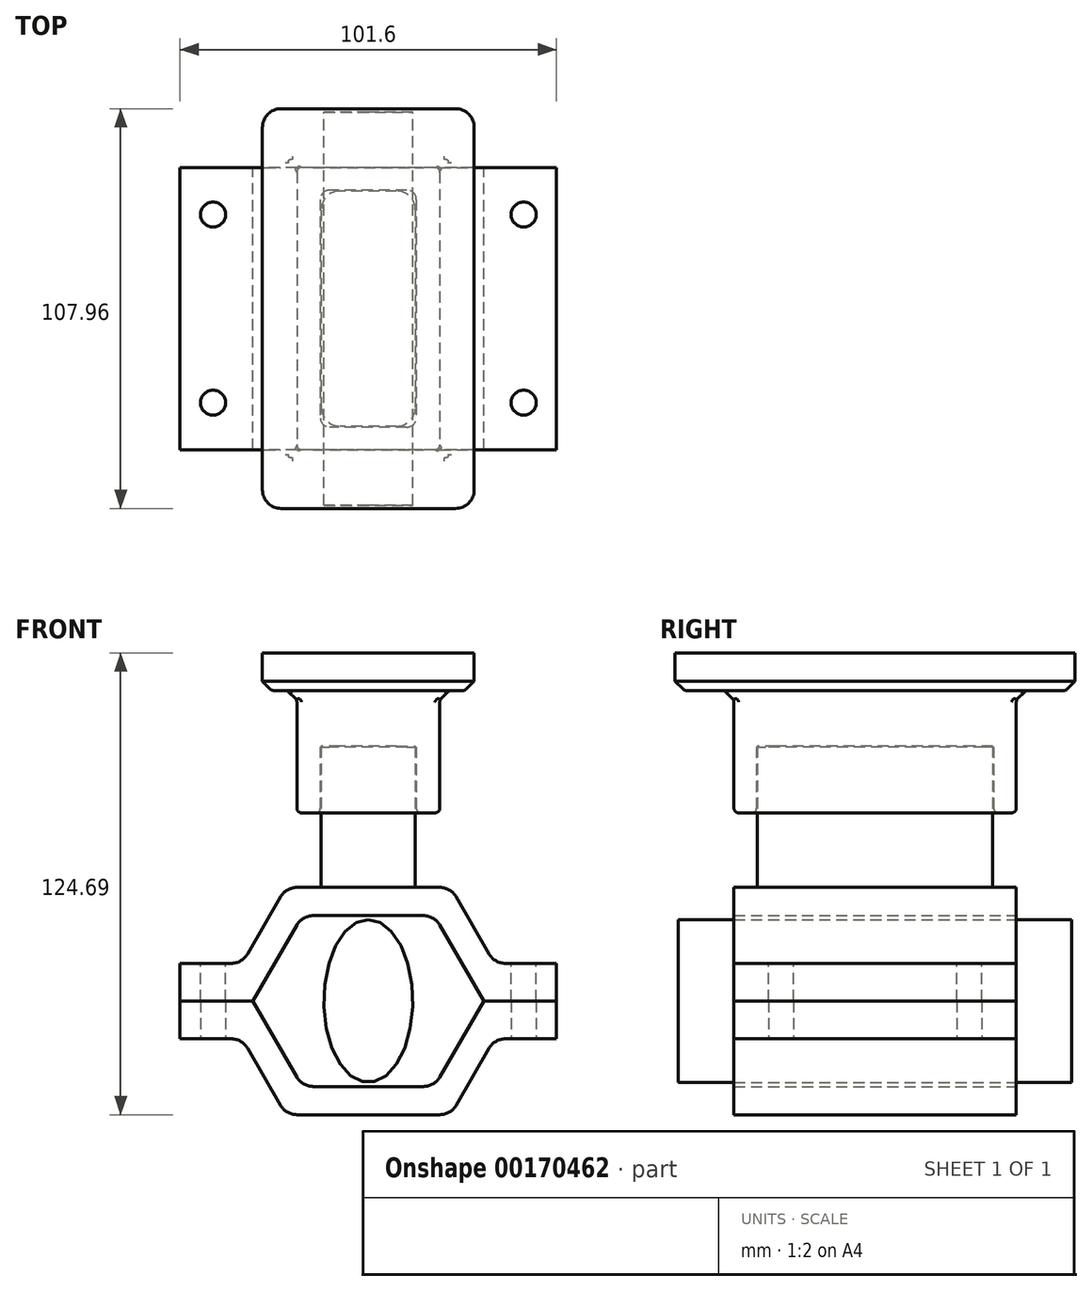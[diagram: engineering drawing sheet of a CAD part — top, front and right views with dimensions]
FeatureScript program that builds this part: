
annotation { "Feature Type Name" : "Feature", "Feature Type Description" : "" }
export const myFeature = defineFeature(function(context is Context, id is Id, definition is map)
    precondition{}
    {
        {
            var Q0;
            Q0=qCreatedBy(makeId("Front.planeOp"),FACE);
            var sketch = newSketch(context, id + "F0", { "sketchPlane" : qUnion([Q0])});
            skLineSegment(sketch, "E0", {"start": v(0, 0) * mm, "end": v(-50.8, 0) * mm});
            skLineSegment(sketch, "E1.MirrorCS", {"start": v(0, 0) * mm, "end": v(50.8, 0) * mm});
            skLineSegment(sketch, "E2", {"start": v(-50.8, 0) * mm, "end": v(-50.8, 10.16) * mm});
            skLineSegment(sketch, "E3", {"start": v(-50.8, 10.16) * mm, "end": v(-34.06, 10.16) * mm});
            skLineSegment(sketch, "E4", {"start": v(-34.06, 10.16) * mm, "end": v(-22.23, 30.66) * mm});
            skLineSegment(sketch, "E5", {"start": v(-22.23, 30.66) * mm, "end": v(0, 30.66) * mm});
            skLineSegment(sketch, "E6.MirrorCS", {"start": v(22.23, 30.66) * mm, "end": v(0, 30.66) * mm});
            skLineSegment(sketch, "E7.MirrorCS", {"start": v(34.06, 10.16) * mm, "end": v(22.23, 30.66) * mm});
            skLineSegment(sketch, "E8.MirrorCS", {"start": v(50.8, 10.16) * mm, "end": v(34.06, 10.16) * mm});
            skLineSegment(sketch, "E9.MirrorCS", {"start": v(50.8, 0) * mm, "end": v(50.8, 10.16) * mm});
            skSolve(sketch);
        }
        {
            var Q0;
            Q0=makeQuery(id+"F0.imprint","IMPRINT",FACE,{"disambiguationData":[TD([[makeQuery(id+"F0.imprint","IMPRINT",EDGE,{"derivedFrom":sQuery(id+"F0.wireOp",EDGE,"E0")}),-1.0]])]});
            extrude(context, id + "F1", {"entities" : qUnion([Q0]), "depth" : 76.2 * mm, "symmetric" : true});
        }
        {
            var Q0;
            Q0=qCreatedBy(makeId("Front.planeOp"),FACE);
            var sketch = newSketch(context, id + "F2", { "sketchPlane" : qUnion([Q0])});
            skLineSegment(sketch, "E10", {"start": v(0, 0) * mm, "end": v(-31.13, 0) * mm});
            skLineSegment(sketch, "E11", {"start": v(-31.13, 0) * mm, "end": v(-17.83, 23.04) * mm});
            skLineSegment(sketch, "E12", {"start": v(-17.83, 23.04) * mm, "end": v(0, 23.04) * mm});
            skLineSegment(sketch, "E13.MirrorCS", {"start": v(17.83, 23.04) * mm, "end": v(0, 23.04) * mm});
            skLineSegment(sketch, "E14.MirrorCS", {"start": v(31.13, 0) * mm, "end": v(17.83, 23.04) * mm});
            skLineSegment(sketch, "E15.MirrorCS", {"start": v(0, 0) * mm, "end": v(31.13, 0) * mm});
            skSolve(sketch);
        }
        {
            var Q0;
            Q0 = qSketchRegion(id + "F2", true);
            extrude(context, id + "F3", {"entities" : qUnion([Q0]), "operationType" : NewBodyOperationType.REMOVE, "endBound" : BoundingType.THROUGH_ALL, "depth" : 25.4 * mm, "hasSecondDirection" : true, "secondDirectionBound" : BoundingType.THROUGH_ALL, "secondDirectionOppositeDirection" : true, "secondDirectionDepth" : 25.4 * mm});
        }
        {
            var Q0;
            Q0=makeQuery(id+"F1.opExtrude","SWEPT_FACE",FACE,{"disambiguationData":[OSD([sQuery(id+"F0.wireOp",EDGE,"E8.MirrorCS")])]});
            var sketch = newSketch(context, id + "F4", { "sketchPlane" : qUnion([Q0])});
            skLineSegment(sketch, "E16.bottom", {"start": v(41.91, 25.4) * mm, "end": v(-41.91, 25.4) * mm, "construction": true});
            skLineSegment(sketch, "E16.top", {"start": v(41.91, -25.4) * mm, "end": v(-41.91, -25.4) * mm, "construction": true});
            skLineSegment(sketch, "E16.left", {"start": v(41.91, 25.4) * mm, "end": v(41.91, -25.4) * mm, "construction": true});
            skLineSegment(sketch, "E16.right", {"start": v(-41.91, 25.4) * mm, "end": v(-41.91, -25.4) * mm, "construction": true});
            skPoint(sketch, "E16.middle", {"position": v(0, 0) * mm});
            skSolve(sketch);
        }
        {
            var Q0;
            Q0=sQuery(id+"F4.wireOp",VERTEX,"E16.left.end");
            var Q1;
            Q1=sQuery(id+"F4.wireOp",VERTEX,"E16.left.start");
            var Q2;
            Q2=sQuery(id+"F4.wireOp",VERTEX,"E16.right.start");
            var Q3;
            Q3=sQuery(id+"F4.wireOp",VERTEX,"E16.top.end");
            var Q4;
            Q4=makeQuery(id+"F1.opExtrude","SWEPT_BODY",BODY,{"disambiguationData":[OSD([sQuery(id+"F0.wireOp",EDGE,"E0"),sQuery(id+"F0.wireOp",EDGE,"E1.MirrorCS"),sQuery(id+"F0.wireOp",EDGE,"E2"),sQuery(id+"F0.wireOp",EDGE,"E3"),sQuery(id+"F0.wireOp",EDGE,"E4"),sQuery(id+"F0.wireOp",EDGE,"E5"),sQuery(id+"F0.wireOp",EDGE,"E6.MirrorCS"),sQuery(id+"F0.wireOp",EDGE,"E7.MirrorCS"),sQuery(id+"F0.wireOp",EDGE,"E8.MirrorCS"),sQuery(id+"F0.wireOp",EDGE,"E9.MirrorCS")])]});
            hole(context, id + "F5", {"style" : HoleStyle.SIMPLE, "endStyle" : HoleEndStyle.THROUGH, "standardTappedOrClearance" : lookupTablePath({ "standard" : "ANSI", "fit" : "Normal (ASME)", "size" : "1/4", "type" : "Clearance" }), "standardBlindInLast" : lookupTablePath({ "fit" : "Free", "standard" : "ANSI", "size" : "1/4", "type" : "Clearance" }), "holeDiameter" : 6.76 * mm, "locations" : qUnion([Q0, Q1, Q2, Q3]), "scope" : qUnion([Q4]), "isTappedThrough" : true});
        }
        {
            var Q0;
            Q0=makeQuery(id+"F1.opExtrude","SWEPT_EDGE",EDGE,{"disambiguationData":[OSD([sQuery(id+"F0.wireOp",EDGE,"E3"),sQuery(id+"F0.wireOp",EDGE,"E4")])]});
            var Q1;
            Q1=makeQuery(id+"F1.opExtrude","SWEPT_EDGE",EDGE,{"disambiguationData":[OSD([sQuery(id+"F0.wireOp",EDGE,"E4"),sQuery(id+"F0.wireOp",EDGE,"E5")])]});
            var Q2;
            Q2=makeQuery(id+"F1.opExtrude","SWEPT_EDGE",EDGE,{"disambiguationData":[OSD([sQuery(id+"F0.wireOp",EDGE,"E6.MirrorCS"),sQuery(id+"F0.wireOp",EDGE,"E7.MirrorCS")])]});
            var Q3;
            Q3=makeQuery(id+"F1.opExtrude","SWEPT_EDGE",EDGE,{"disambiguationData":[OSD([sQuery(id+"F0.wireOp",EDGE,"E7.MirrorCS"),sQuery(id+"F0.wireOp",EDGE,"E8.MirrorCS")])]});
            var Q4;
            Q4=makeQuery(id+"F3.boolean.opBoolean","COPY",EDGE,{"derivedFrom":makeQuery(id+"F3.opExtrude","SWEPT_EDGE",EDGE,{"disambiguationData":[OSD([sQuery(id+"F2.wireOp",EDGE,"E11"),sQuery(id+"F2.wireOp",EDGE,"E12")])]})});
            var Q5;
            Q5=makeQuery(id+"F3.boolean.opBoolean","COPY",EDGE,{"derivedFrom":makeQuery(id+"F3.opExtrude","SWEPT_EDGE",EDGE,{"disambiguationData":[OSD([sQuery(id+"F2.wireOp",EDGE,"E13.MirrorCS"),sQuery(id+"F2.wireOp",EDGE,"E14.MirrorCS")])]})});
            var Q6;
            Q6=makeQuery(id+"F3.boolean.opBoolean","COPY",EDGE,{"derivedFrom":makeQuery(id+"F3.opExtrude","SWEPT_EDGE",EDGE,{"disambiguationData":[OSD([sQuery(id+"F2.wireOp",EDGE,"E10"),sQuery(id+"F2.wireOp",EDGE,"E11")])]})});
            var Q7;
            Q7=makeQuery(id+"F3.boolean.opBoolean","COPY",EDGE,{"derivedFrom":makeQuery(id+"F3.opExtrude","SWEPT_EDGE",EDGE,{"disambiguationData":[OSD([sQuery(id+"F2.wireOp",EDGE,"E14.MirrorCS"),sQuery(id+"F2.wireOp",EDGE,"E15.MirrorCS")])]})});
            fillet(context, id + "F6", {"entities" : qUnion([Q0, Q1, Q2, Q3, Q4, Q5, Q6, Q7]), "radius" : 5.08 * mm, "tangentPropagation" : true, "allowEdgeOverflow" : false});
        }
        {
            var Q0;
            Q0=qCreatedBy(makeId("Top.planeOp"),FACE);
            cPlane(context, id + "F7", {"entities" : qUnion([Q0]), "cplaneType" : CPlaneType.OFFSET, "offset" : 0.03 * mm, "oppositeDirection" : true, "width" : 152.4 * mm, "height" : 152.4 * mm});
        }
        {
            var Q0;
            Q0=makeQuery(id+"F1.opExtrude","SWEPT_BODY",BODY,{"disambiguationData":[OSD([sQuery(id+"F0.wireOp",EDGE,"E0"),sQuery(id+"F0.wireOp",EDGE,"E1.MirrorCS"),sQuery(id+"F0.wireOp",EDGE,"E2"),sQuery(id+"F0.wireOp",EDGE,"E3"),sQuery(id+"F0.wireOp",EDGE,"E4"),sQuery(id+"F0.wireOp",EDGE,"E5"),sQuery(id+"F0.wireOp",EDGE,"E6.MirrorCS"),sQuery(id+"F0.wireOp",EDGE,"E7.MirrorCS"),sQuery(id+"F0.wireOp",EDGE,"E8.MirrorCS"),sQuery(id+"F0.wireOp",EDGE,"E9.MirrorCS")])]});
            var Q1;
            Q1=qCreatedBy(id+"F7.planeOp",FACE);
            mirror(context, id + "F8", {"entities" : qUnion([Q0]), "mirrorPlane" : qUnion([Q1])});
        }
        {
            var Q0;
            Q0=makeQuery(id+"F1.opExtrude","SWEPT_FACE",FACE,{"disambiguationData":[OSD([sQuery(id+"F0.wireOp",EDGE,"E5"),sQuery(id+"F0.wireOp",EDGE,"E6.MirrorCS")])]});
            var sketch = newSketch(context, id + "F9", { "sketchPlane" : qUnion([Q0])});
            skLineSegment(sketch, "E17.bottom", {"start": v(12.7, 31.75) * mm, "end": v(-12.7, 31.75) * mm});
            skLineSegment(sketch, "E17.top", {"start": v(12.7, -31.75) * mm, "end": v(-12.7, -31.75) * mm});
            skLineSegment(sketch, "E17.left", {"start": v(12.7, 31.75) * mm, "end": v(12.7, -31.75) * mm});
            skLineSegment(sketch, "E17.right", {"start": v(-12.7, 31.75) * mm, "end": v(-12.7, -31.75) * mm});
            skPoint(sketch, "E17.middle", {"position": v(0, 0) * mm});
            skSolve(sketch);
        }
        {
            var Q0;
            Q0=makeQuery(id+"F9.imprint","IMPRINT",FACE,{"disambiguationData":[TD([[makeQuery(id+"F9.imprint","IMPRINT",EDGE,{"derivedFrom":sQuery(id+"F9.wireOp",EDGE,"E17.bottom")}),1.0]])]});
            extrude(context, id + "F10", {"entities" : qUnion([Q0]), "operationType" : NewBodyOperationType.ADD, "depth" : 38.1 * mm});
        }
        {
            var Q0;
            Q0=qCreatedBy(makeId("Top.planeOp"),FACE);
            cPlane(context, id + "F11", {"entities" : qUnion([Q0]), "cplaneType" : CPlaneType.OFFSET, "offset" : 50.8 * mm, "width" : 152.4 * mm, "height" : 152.4 * mm});
        }
        {
            var Q0;
            Q0=qCreatedBy(id+"F11.planeOp",FACE);
            var sketch = newSketch(context, id + "F12", { "sketchPlane" : qUnion([Q0])});
            skLineSegment(sketch, "E18.bottom", {"start": v(12.95, 32) * mm, "end": v(-12.95, 32) * mm});
            skLineSegment(sketch, "E18.top", {"start": v(12.95, -32) * mm, "end": v(-12.95, -32) * mm});
            skLineSegment(sketch, "E18.left", {"start": v(12.95, 32) * mm, "end": v(12.95, -32) * mm});
            skLineSegment(sketch, "E18.right", {"start": v(-12.95, 32) * mm, "end": v(-12.95, -32) * mm});
            skPoint(sketch, "E18.middle", {"position": v(0, 0) * mm});
            skLineSegment(sketch, "E19.bottom", {"start": v(19.3, 38.1) * mm, "end": v(-19.3, 38.1) * mm});
            skLineSegment(sketch, "E19.top", {"start": v(19.3, -38.1) * mm, "end": v(-19.3, -38.1) * mm});
            skLineSegment(sketch, "E19.left", {"start": v(19.3, 38.1) * mm, "end": v(19.3, -38.1) * mm});
            skLineSegment(sketch, "E19.right", {"start": v(-19.3, 38.1) * mm, "end": v(-19.3, -38.1) * mm});
            skSolve(sketch);
        }
        {
            var Q0;
            Q0 = qSketchRegion(id + "F12", true);
            extrude(context, id + "F13", {"entities" : qUnion([Q0]), "depth" : 38.1 * mm});
        }
        {
            var Q0;
            Q0=makeQuery(id+"F13.opExtrude","CAP_FACE",FACE,{"disambiguationData":[OSD([sQuery(id+"F12.wireOp",EDGE,"E18.bottom"),sQuery(id+"F12.wireOp",EDGE,"E18.top"),sQuery(id+"F12.wireOp",EDGE,"E18.left"),sQuery(id+"F12.wireOp",EDGE,"E18.right"),sQuery(id+"F12.wireOp",EDGE,"E19.bottom"),sQuery(id+"F12.wireOp",EDGE,"E19.top"),sQuery(id+"F12.wireOp",EDGE,"E19.left"),sQuery(id+"F12.wireOp",EDGE,"E19.right")])],"isStart":false});
            var sketch = newSketch(context, id + "F14", { "sketchPlane" : qUnion([Q0])});
            skLineSegment(sketch, "E20.0", {"start": v(12.95, 32) * mm, "end": v(-12.95, 32) * mm});
            skLineSegment(sketch, "E21.0", {"start": v(-12.95, 32) * mm, "end": v(-12.95, -32) * mm});
            skLineSegment(sketch, "E22.0", {"start": v(12.95, -32) * mm, "end": v(-12.95, -32) * mm});
            skLineSegment(sketch, "E23.0", {"start": v(12.95, 32) * mm, "end": v(12.95, -32) * mm});
            skSolve(sketch);
        }
        {
            var Q0;
            Q0=makeQuery(id+"F14.imprint","IMPRINT",FACE,{"disambiguationData":[TD([[makeQuery(id+"F14.imprint","IMPRINT",EDGE,{"derivedFrom":sQuery(id+"F14.wireOp",EDGE,"E20.0")}),1.0]])]});
            extrude(context, id + "F15", {"entities" : qUnion([Q0]), "oppositeDirection" : true, "depth" : 20.32 * mm});
        }
        {
            var Q0;
            Q0=makeQuery(id+"F15.opExtrude","SWEPT_BODY",BODY,{"disambiguationData":[OSD([sQuery(id+"F14.wireOp",EDGE,"E20.0"),sQuery(id+"F14.wireOp",EDGE,"E21.0"),sQuery(id+"F14.wireOp",EDGE,"E22.0"),sQuery(id+"F14.wireOp",EDGE,"E23.0")])]});
            var Q1;
            Q1=makeQuery(id+"F13.opExtrude","SWEPT_BODY",BODY,{"disambiguationData":[OSD([sQuery(id+"F12.wireOp",EDGE,"E18.bottom"),sQuery(id+"F12.wireOp",EDGE,"E18.top"),sQuery(id+"F12.wireOp",EDGE,"E18.left"),sQuery(id+"F12.wireOp",EDGE,"E18.right"),sQuery(id+"F12.wireOp",EDGE,"E19.bottom"),sQuery(id+"F12.wireOp",EDGE,"E19.top"),sQuery(id+"F12.wireOp",EDGE,"E19.left"),sQuery(id+"F12.wireOp",EDGE,"E19.right")])]});
            booleanBodies(context, id + "F16", {"operationType" : BooleanOperationType.UNION, "tools" : qUnion([Q0, Q1])});
        }
        {
            var Q0;
            Q0=makeQuery(id+"F16.opBoolean","MERGE",FACE,{"derivedFrom":[makeQuery(id+"F13.opExtrude","CAP_FACE",FACE,{"disambiguationData":[OSD([sQuery(id+"F12.wireOp",EDGE,"E18.bottom"),sQuery(id+"F12.wireOp",EDGE,"E18.top"),sQuery(id+"F12.wireOp",EDGE,"E18.left"),sQuery(id+"F12.wireOp",EDGE,"E18.right"),sQuery(id+"F12.wireOp",EDGE,"E19.bottom"),sQuery(id+"F12.wireOp",EDGE,"E19.top"),sQuery(id+"F12.wireOp",EDGE,"E19.left"),sQuery(id+"F12.wireOp",EDGE,"E19.right")])],"isStart":false}),makeQuery(id+"F15.opExtrude","CAP_FACE",FACE,{"disambiguationData":[OSD([sQuery(id+"F14.wireOp",EDGE,"E20.0"),sQuery(id+"F14.wireOp",EDGE,"E21.0"),sQuery(id+"F14.wireOp",EDGE,"E22.0"),sQuery(id+"F14.wireOp",EDGE,"E23.0")])],"isStart":true})]});
            var sketch = newSketch(context, id + "F17", { "sketchPlane" : qUnion([Q0])});
            skLineSegment(sketch, "E24.bottom", {"start": v(28.58, -53.98) * mm, "end": v(-28.57, -53.98) * mm});
            skLineSegment(sketch, "E24.top", {"start": v(28.57, 53.98) * mm, "end": v(-28.58, 53.98) * mm});
            skLineSegment(sketch, "E24.left", {"start": v(28.58, -53.98) * mm, "end": v(28.57, 53.98) * mm});
            skLineSegment(sketch, "E24.right", {"start": v(-28.57, -53.98) * mm, "end": v(-28.58, 53.97) * mm});
            skPoint(sketch, "E24.middle", {"position": v(0, 0) * mm});
            skSolve(sketch);
        }
        {
            var Q0;
            Q0 = qSketchRegion(id + "F17", true);
            extrude(context, id + "F18", {"entities" : qUnion([Q0]), "depth" : 5.08 * mm, "hasSecondDirection" : true, "secondDirectionOppositeDirection" : true, "secondDirectionDepth" : 5.08 * mm});
        }
        {
            var Q0;
            Q0=makeQuery(id+"F15.opExtrude","SWEPT_BODY",BODY,{"disambiguationData":[OSD([sQuery(id+"F14.wireOp",EDGE,"E20.0"),sQuery(id+"F14.wireOp",EDGE,"E21.0"),sQuery(id+"F14.wireOp",EDGE,"E22.0"),sQuery(id+"F14.wireOp",EDGE,"E23.0")])]});
            var Q1;
            Q1=makeQuery(id+"F18.opExtrude","SWEPT_BODY",BODY,{"disambiguationData":[OSD([sQuery(id+"F17.wireOp",EDGE,"E24.bottom"),sQuery(id+"F17.wireOp",EDGE,"E24.top"),sQuery(id+"F17.wireOp",EDGE,"E24.left"),sQuery(id+"F17.wireOp",EDGE,"E24.right")])]});
            booleanBodies(context, id + "F19", {"operationType" : BooleanOperationType.UNION, "tools" : qUnion([Q0, Q1])});
        }
        {
            var Q0;
            Q0=makeQuery(id+"F18.opExtrude","SWEPT_EDGE",EDGE,{"disambiguationData":[OSD([sQuery(id+"F17.wireOp",EDGE,"E24.bottom"),sQuery(id+"F17.wireOp",EDGE,"E24.left")])]});
            var Q1;
            Q1=makeQuery(id+"F18.opExtrude","SWEPT_EDGE",EDGE,{"disambiguationData":[OSD([sQuery(id+"F17.wireOp",EDGE,"E24.bottom"),sQuery(id+"F17.wireOp",EDGE,"E24.right")])]});
            var Q2;
            Q2=makeQuery(id+"F18.opExtrude","SWEPT_EDGE",EDGE,{"disambiguationData":[OSD([sQuery(id+"F17.wireOp",EDGE,"E24.top"),sQuery(id+"F17.wireOp",EDGE,"E24.left")])]});
            var Q3;
            Q3=makeQuery(id+"F18.opExtrude","SWEPT_EDGE",EDGE,{"disambiguationData":[OSD([sQuery(id+"F17.wireOp",EDGE,"E24.top"),sQuery(id+"F17.wireOp",EDGE,"E24.right")])]});
            fillet(context, id + "F20", {"entities" : qUnion([Q0, Q1, Q2, Q3]), "radius" : 5.08 * mm, "tangentPropagation" : true, "allowEdgeOverflow" : false});
        }
        {
            var Q0;
            Q0=makeQuery(id+"F18.opExtrude","CAP_FACE",FACE,{"disambiguationData":[OSD([sQuery(id+"F17.wireOp",EDGE,"E24.bottom"),sQuery(id+"F17.wireOp",EDGE,"E24.top"),sQuery(id+"F17.wireOp",EDGE,"E24.left"),sQuery(id+"F17.wireOp",EDGE,"E24.right")])],"isStart":true});
            chamfer(context, id + "F21", {"entities" : qUnion([Q0]), "width" : 2.54 * mm, "tangentPropagation" : true});
        }
        {
            var Q0;
            Q0=makeQuery(id+"F10.opExtrude","SWEPT_EDGE",EDGE,{"disambiguationData":[OSD([sQuery(id+"F9.wireOp",EDGE,"E17.top"),sQuery(id+"F9.wireOp",EDGE,"E17.left")])]});
            var Q1;
            Q1=makeQuery(id+"F10.opExtrude","SWEPT_EDGE",EDGE,{"disambiguationData":[OSD([sQuery(id+"F9.wireOp",EDGE,"E17.top"),sQuery(id+"F9.wireOp",EDGE,"E17.right")])]});
            var Q2;
            Q2=makeQuery(id+"F10.opExtrude","SWEPT_EDGE",EDGE,{"disambiguationData":[OSD([sQuery(id+"F9.wireOp",EDGE,"E17.bottom"),sQuery(id+"F9.wireOp",EDGE,"E17.left")])]});
            var Q3;
            Q3=makeQuery(id+"F10.opExtrude","SWEPT_EDGE",EDGE,{"disambiguationData":[OSD([sQuery(id+"F9.wireOp",EDGE,"E17.bottom"),sQuery(id+"F9.wireOp",EDGE,"E17.right")])]});
            fillet(context, id + "F22", {"entities" : qUnion([Q0, Q1, Q2, Q3]), "radius" : 5.08 * mm, "tangentPropagation" : true, "allowEdgeOverflow" : false});
        }
        {
            var Q0;
            Q0=makeQuery(id+"F13.opExtrude","SWEPT_EDGE",EDGE,{"disambiguationData":[OSD([sQuery(id+"F12.wireOp",EDGE,"E18.bottom"),sQuery(id+"F12.wireOp",EDGE,"E18.right")])]});
            var Q1;
            Q1=makeQuery(id+"F13.opExtrude","SWEPT_EDGE",EDGE,{"disambiguationData":[OSD([sQuery(id+"F12.wireOp",EDGE,"E18.bottom"),sQuery(id+"F12.wireOp",EDGE,"E18.left")])]});
            var Q2;
            Q2=makeQuery(id+"F13.opExtrude","SWEPT_EDGE",EDGE,{"disambiguationData":[OSD([sQuery(id+"F12.wireOp",EDGE,"E18.top"),sQuery(id+"F12.wireOp",EDGE,"E18.right")])]});
            var Q3;
            Q3=makeQuery(id+"F13.opExtrude","SWEPT_EDGE",EDGE,{"disambiguationData":[OSD([sQuery(id+"F12.wireOp",EDGE,"E18.top"),sQuery(id+"F12.wireOp",EDGE,"E18.left")])]});
            fillet(context, id + "F23", {"entities" : qUnion([Q0, Q1, Q2, Q3]), "radius" : 2.54 * mm, "tangentPropagation" : true, "allowEdgeOverflow" : false});
        }
        {
            var Q0;
            Q0=makeQuery(id+"F13.opExtrude","SWEPT_FACE",FACE,{"disambiguationData":[OSD([sQuery(id+"F12.wireOp",EDGE,"E19.left")])]});
            var Q1;
            Q1=makeQuery(id+"F13.opExtrude","SWEPT_FACE",FACE,{"disambiguationData":[OSD([sQuery(id+"F12.wireOp",EDGE,"E19.top")])]});
            var Q2;
            Q2=makeQuery(id+"F13.opExtrude","CAP_FACE",FACE,{"disambiguationData":[OSD([sQuery(id+"F12.wireOp",EDGE,"E18.bottom"),sQuery(id+"F12.wireOp",EDGE,"E18.top"),sQuery(id+"F12.wireOp",EDGE,"E18.left"),sQuery(id+"F12.wireOp",EDGE,"E18.right"),sQuery(id+"F12.wireOp",EDGE,"E19.bottom"),sQuery(id+"F12.wireOp",EDGE,"E19.top"),sQuery(id+"F12.wireOp",EDGE,"E19.left"),sQuery(id+"F12.wireOp",EDGE,"E19.right")])],"isStart":true});
            var Q3;
            Q3=makeQuery(id+"F13.opExtrude","SWEPT_FACE",FACE,{"disambiguationData":[OSD([sQuery(id+"F12.wireOp",EDGE,"E19.right")])]});
            var Q4;
            Q4=makeQuery(id+"F13.opExtrude","SWEPT_FACE",FACE,{"disambiguationData":[OSD([sQuery(id+"F12.wireOp",EDGE,"E19.bottom")])]});
            var Q5;
            Q5=makeQuery(id+"F21.opChamfer","BLEND_FACE",FACE,{"disambiguationData":[OSD([sQuery(id+"F12.wireOp",EDGE,"E19.right"),sQuery(id+"F17.wireOp",EDGE,"E24.bottom"),sQuery(id+"F17.wireOp",EDGE,"E24.top"),sQuery(id+"F17.wireOp",EDGE,"E24.left"),sQuery(id+"F17.wireOp",EDGE,"E24.right")])]});
            var Q6;
            Q6=makeQuery(id+"F21.opChamfer","BLEND_FACE",FACE,{"disambiguationData":[OSD([sQuery(id+"F12.wireOp",EDGE,"E19.top"),sQuery(id+"F17.wireOp",EDGE,"E24.bottom"),sQuery(id+"F17.wireOp",EDGE,"E24.top"),sQuery(id+"F17.wireOp",EDGE,"E24.left"),sQuery(id+"F17.wireOp",EDGE,"E24.right")])]});
            var Q7;
            Q7=makeQuery(id+"F18.opExtrude","CAP_FACE",FACE,{"disambiguationData":[OSD([sQuery(id+"F17.wireOp",EDGE,"E24.bottom"),sQuery(id+"F17.wireOp",EDGE,"E24.top"),sQuery(id+"F17.wireOp",EDGE,"E24.left"),sQuery(id+"F17.wireOp",EDGE,"E24.right")])],"isStart":true});
            var Q8;
            {var subQ0=makeQuery(id+"F18.opExtrude","CAP_FACE",FACE,{"disambiguationData":[OSD([sQuery(id+"F17.wireOp",EDGE,"E24.bottom"),sQuery(id+"F17.wireOp",EDGE,"E24.top"),sQuery(id+"F17.wireOp",EDGE,"E24.left"),sQuery(id+"F17.wireOp",EDGE,"E24.right")])],"isStart":true});Q8=makeQuery(id+"F21.opChamfer","BLEND_EDGE",EDGE,{"blendedFrom":[makeQuery(id+"F19.opBoolean","INTERSECT",EDGE,{"derivedFrom":[makeQuery(id+"F13.opExtrude","SWEPT_FACE",FACE,{"disambiguationData":[OSD([sQuery(id+"F12.wireOp",EDGE,"E19.bottom")])]}),subQ0]}),makeQuery(id+"F19.opBoolean","INTERSECT",EDGE,{"derivedFrom":[makeQuery(id+"F13.opExtrude","SWEPT_FACE",FACE,{"disambiguationData":[OSD([sQuery(id+"F12.wireOp",EDGE,"E19.left")])]}),subQ0]})],"blendedInto":[]});}
            fillet(context, id + "F24", {"entities" : qUnion([Q0, Q1, Q2, Q3, Q4, Q5, Q6, Q7, Q8]), "radius" : 1.27 * mm, "tangentPropagation" : true, "allowEdgeOverflow" : false});
        }
        {
            var Q0;
            Q0=qCreatedBy(makeId("Front.planeOp"),FACE);
            var sketch = newSketch(context, id + "F25", { "sketchPlane" : qUnion([Q0])});
            skEllipse(sketch, "E25", {"center": v(0, 0) * mm, "majorRadius": 22 * mm, "minorRadius": 12 * mm, "majorAxis": v(0, 1)});
            skSolve(sketch);
        }
        {
            var Q0;
            Q0=makeQuery(id+"F25.imprint","IMPRINT",FACE,{"disambiguationData":[TD([[makeQuery(id+"F25.imprint","IMPRINT",EDGE,{"derivedFrom":sQuery(id+"F25.wireOp",EDGE,"E25")}),1.0]])]});
            extrude(context, id + "F26", {"entities" : qUnion([Q0]), "depth" : 106.17 * mm, "symmetric" : true});
        }
    });
